# Revit family: Electrical-Teknion-NBAJ_Banqs_Small_Power_Flip-R2019
name_source: partatom
category: Furniture
units: mm (PartAtom-declared; Revit-internal decimal feet)

## family parameters
Always vertical = Yes
Cut with Voids When Loaded = No
OmniClass Number = 23.40.20.00
OmniClass Title = General Furniture and Specialties
Room Calculation Point = No
Shared = Yes
Work Plane-Based = No

## types (2) — shared parameters
Assembly Code = E2020200
Manufacturer = Teknion
Manufacturer Fax = 416.661.4586
Part Number = NBAJ
Product Documentation Link = https://www.teknion.com
Product Line = Bnaqs
Product Page URL = https://www.teknion.com
Series = Soft Seating
Sustainability Data = https://www.teknion.com
URL = www.teknion.com
Unit Weight URL = http://www.teknion.com
Warranty = http://www.teknion.com
zero-valued in all types: Default Elevation

## per-type parameters (varying)
| type | Description | Electrical Finishes | Model |
| Banqs Small Power Flip in White | Banqs Small Power Flip, 1-Power, 1-USB-A, 1-USB-C and No-Data Opening, White Finish | Plastic - Teknion - 8C - Very White | NBAJD1110W |
| Banqs Small Power Flip in Black | Banqs Small Power Flip, 1-Power, 1-USB-A, 1-USB-C and No-Data Opening, Black Finish | Plastic - Teknion - E - Ebony | NBAJD1110B |

## geometry (parser evidence)
native form markers: Sweep x3
no freeform markers — native parametric forms only
